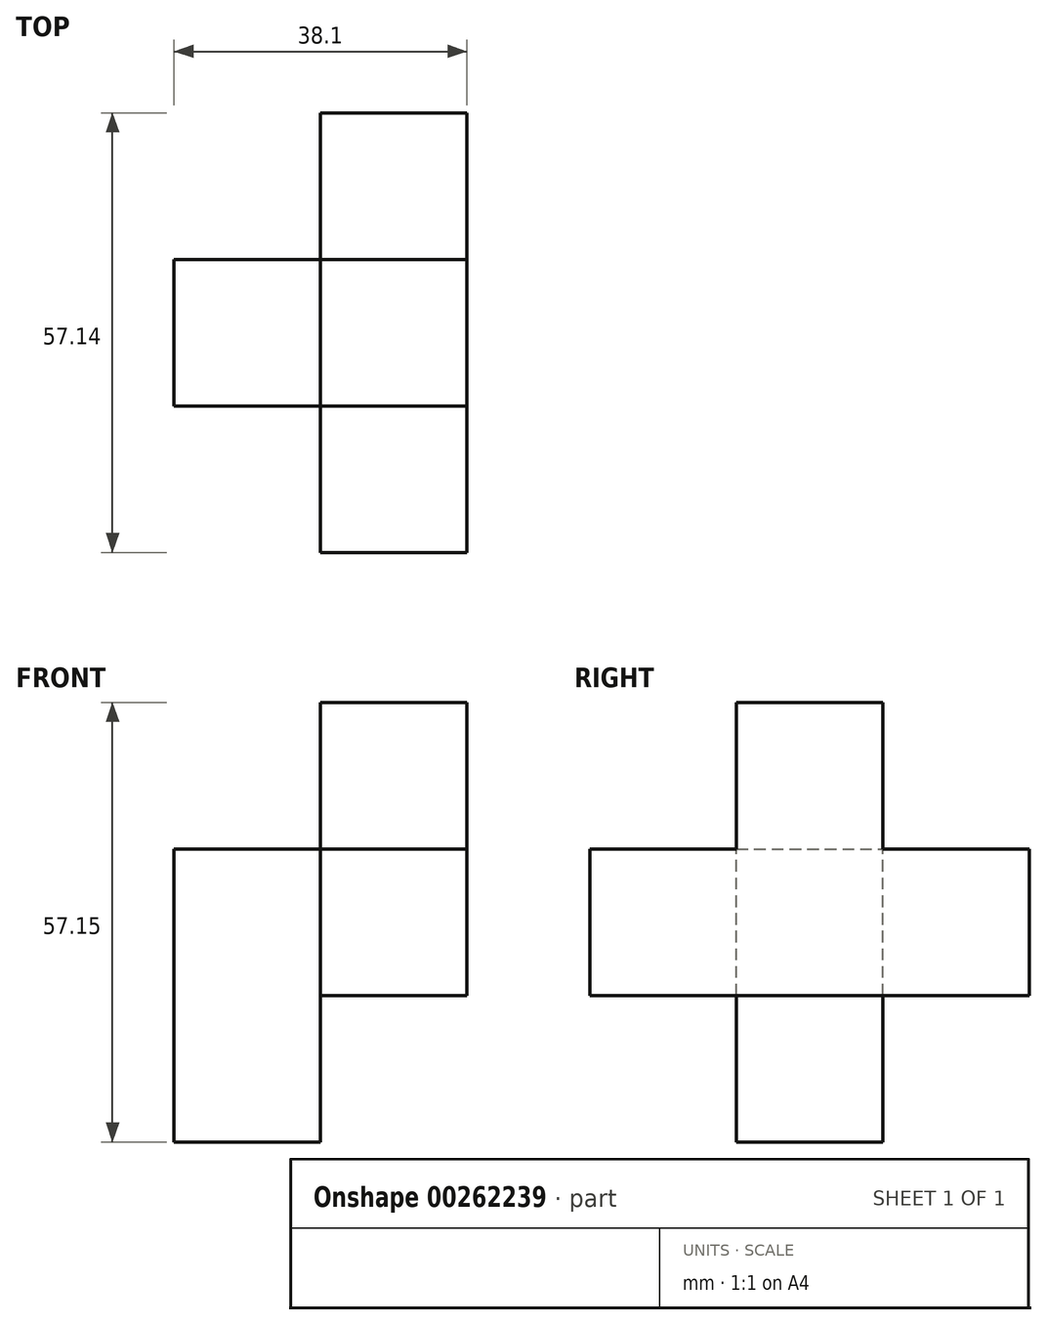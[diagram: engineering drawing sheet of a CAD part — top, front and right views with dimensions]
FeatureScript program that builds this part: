
annotation { "Feature Type Name" : "Feature", "Feature Type Description" : "" }
export const myFeature = defineFeature(function(context is Context, id is Id, definition is map)
    precondition{}
    {
        {
            var Q0;
            Q0=qCreatedBy(makeId("Front.planeOp"),FACE);
            var sketch = newSketch(context, id + "F0", { "sketchPlane" : qUnion([Q0])});
            skLineSegment(sketch, "E0.bottom", {"start": v(-68.56, 60.56) * mm, "end": v(-49.5, 60.56) * mm});
            skLineSegment(sketch, "E0.top", {"start": v(-68.56, 41.5) * mm, "end": v(-49.5, 41.5) * mm});
            skLineSegment(sketch, "E0.left", {"start": v(-68.56, 60.56) * mm, "end": v(-68.56, 41.5) * mm});
            skLineSegment(sketch, "E0.right", {"start": v(-49.5, 60.56) * mm, "end": v(-49.5, 41.5) * mm});
            skLineSegment(sketch, "E1", {"start": v(-49.5, 60.56) * mm, "end": v(-49.5, 79.6) * mm});
            skLineSegment(sketch, "E2", {"start": v(-49.5, 79.6) * mm, "end": v(-30.46, 79.6) * mm});
            skLineSegment(sketch, "E3", {"start": v(-49.5, 41.5) * mm, "end": v(-30.46, 41.5) * mm});
            skLineSegment(sketch, "E4", {"start": v(-30.46, 41.5) * mm, "end": v(-30.46, 79.6) * mm});
            skLineSegment(sketch, "E5", {"start": v(-68.56, 41.5) * mm, "end": v(-68.56, 22.46) * mm});
            skLineSegment(sketch, "E6", {"start": v(-68.56, 22.46) * mm, "end": v(-49.5, 22.46) * mm});
            skLineSegment(sketch, "E7", {"start": v(-49.5, 22.46) * mm, "end": v(-49.5, 41.5) * mm});
            skLineSegment(sketch, "E8", {"start": v(-49.5, 60.56) * mm, "end": v(-30.46, 60.56) * mm});
            skPoint(sketch, "E8.endSnap0", {"position": v(-30.46, 60.56) * mm});
            skSolve(sketch);
        }
        {
            var Q0;
            Q0=makeQuery(id+"F0.imprint","IMPRINT",FACE,{"disambiguationData":[TD([[makeQuery(id+"F0.imprint","IMPRINT",EDGE,{"derivedFrom":sQuery(id+"F0.wireOp",EDGE,"E0.top")}),-1.0]])]});
            var Q1;
            Q1=makeQuery(id+"F0.imprint","IMPRINT",FACE,{"disambiguationData":[TD([[makeQuery(id+"F0.imprint","IMPRINT",EDGE,{"derivedFrom":sQuery(id+"F0.wireOp",EDGE,"E0.bottom")}),-1.0]])]});
            var Q2;
            Q2=makeQuery(id+"F0.imprint","IMPRINT",FACE,{"disambiguationData":[TD([[makeQuery(id+"F0.imprint","IMPRINT",EDGE,{"derivedFrom":sQuery(id+"F0.wireOp",EDGE,"E1")}),-1.0]])]});
            extrude(context, id + "F1", {"entities" : qUnion([Q0, Q1, Q2]), "endBound" : BoundingType.SYMMETRIC, "depth" : 19.05 * mm});
        }
        {
            var Q0;
            Q0=makeQuery(id+"F0.imprint","IMPRINT",FACE,{"disambiguationData":[TD([[makeQuery(id+"F0.imprint","IMPRINT",EDGE,{"derivedFrom":sQuery(id+"F0.wireOp",EDGE,"E0.right")}),1.0]])]});
            extrude(context, id + "F2", {"entities" : qUnion([Q0]), "operationType" : NewBodyOperationType.ADD, "endBound" : BoundingType.SYMMETRIC, "depth" : 57.15 * mm});
        }
    });
